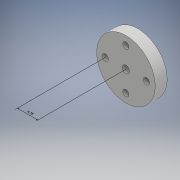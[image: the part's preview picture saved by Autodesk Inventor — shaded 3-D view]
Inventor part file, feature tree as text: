
AUTODESK INVENTOR PART (.ipt)
format: ipt  version: 2018 (Build 220112000, 112)  size: 404,480 bytes
history: native  units: mm
features: extrude x5, sketch x5, other x2, projected_geometry x1
ambient origin geometry x8: Origin, YZ Plane, XZ Plane, XY Plane, X Axis, Y Axis, Z Axis, Center Point
bodies: Solide1 (feature_tree)
feature tree (13):
  other  "Annotations"
  extrude  "Extrusion1"  Depth=22.0mm
  extrude  "Extrusion2"  Depth=7.75mm
  extrude  "Extrusion3"  Depth=2.3mm
  extrude  "Extrusion4"  Depth=3.9mm
  extrude  "Extrusion5"  Depth=40.0mm TaperAngle=360.0deg
  sketch  "Esquisse1"
  sketch  "Esquisse2"
  sketch  "Esquisse3"
  sketch  "Esquisse4"
  projected_geometry  "Boucle projetée1"
  sketch  "Esquisse5"
  other  "Cote linéaire 1"
